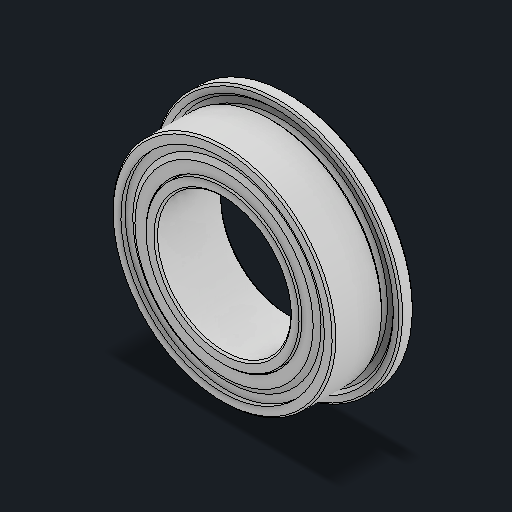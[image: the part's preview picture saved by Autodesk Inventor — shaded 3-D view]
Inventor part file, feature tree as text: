
AUTODESK INVENTOR PART (.ipt)
format: ipt  version: 2024 (Build 280153000, 153)  size: 833,024 bytes
history: native  units: in
note: dims shown in document units (in); Inventor stores cm internally (conversion verified against a paired STEP export)
features: other x18, revolve x3
ambient origin geometry x8: Origin, YZ Plane, XZ Plane, XY Plane, X Axis, Y Axis, Z Axis, Center Point
bodies: Solid1 (feature_tree), Solid2 (feature_tree), Solid3 (feature_tree), Solid4 (feature_tree), Solid5 (feature_tree), Solid6 (feature_tree), Solid7 (feature_tree), Solid8 (feature_tree), Solid9 (feature_tree), Solid10 (feature_tree), Solid11 (feature_tree), Solid12 (feature_tree), Solid13 (feature_tree), Solid14 (feature_tree), Solid15 (feature_tree), Solid16 (feature_tree), Solid17 (feature_tree), Solid18 (feature_tree), Solid19 (feature_tree), Solid20 (feature_tree), Solid21 (feature_tree)
feature tree (21):
  revolve  "Revolve3"  [1 undecoded]
  other  "CirPattern3[1]"
  other  "CirPattern3[2]"
  other  "CirPattern3[3]"
  other  "CirPattern3[4]"
  other  "CirPattern3[5]"
  other  "CirPattern3[6]"
  other  "CirPattern3[7]"
  other  "CirPattern3[8]"
  other  "CirPattern3[9]"
  other  "CirPattern3[10]"
  other  "CirPattern3[11]"
  other  "Cut-Revolve1[1]"
  other  "Cut-Revolve1[2]"
  revolve  "Revolve4[1]"  [1 undecoded]
  revolve  "Revolve4[2]"  [1 undecoded]
  other  "CirPattern3[12]"
  other  "CirPattern3[13]"
  other  "CirPattern3[14]"
  other  "CirPattern3[15]"
  other  "CirPattern3[16]"
note: 3 required parameter values undecoded (feature->parameter linkage not recoverable at this tier; creation-order binding heuristic only, values carry confidence <= 0.55)
